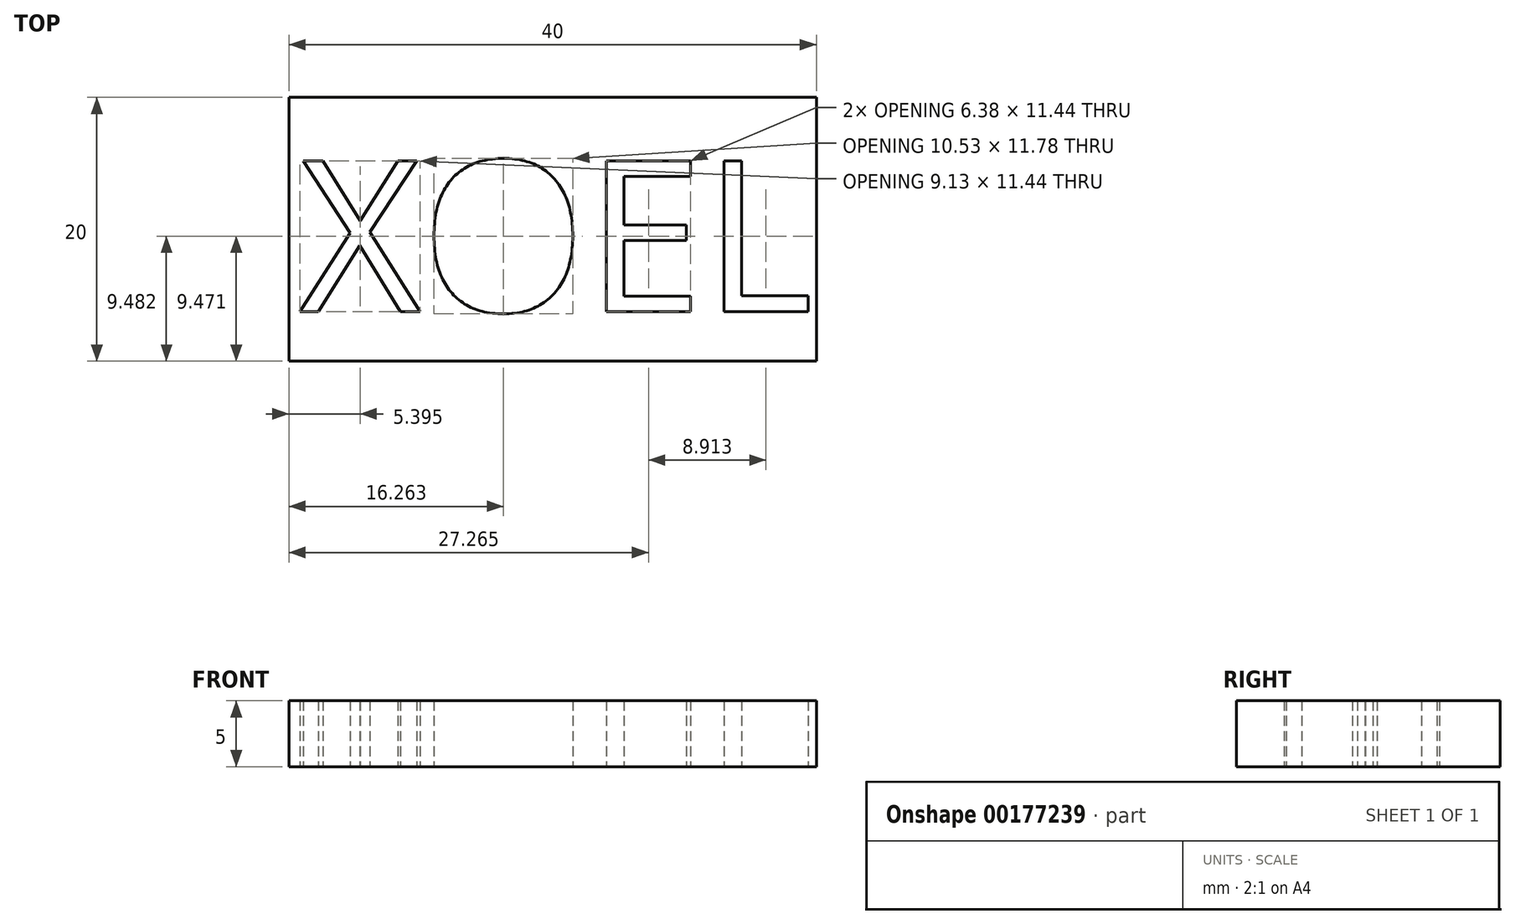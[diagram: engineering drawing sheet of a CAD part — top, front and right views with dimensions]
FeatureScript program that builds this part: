
annotation { "Feature Type Name" : "Feature", "Feature Type Description" : "" }
export const myFeature = defineFeature(function(context is Context, id is Id, definition is map)
    precondition{}
    {
        {
            var Q0;
            Q0=qCreatedBy(makeId("Top.planeOp"),FACE);
            var sketch = newSketch(context, id + "F0", { "sketchPlane" : qUnion([Q0])});
            skLineSegment(sketch, "E0.bottom", {"start": v(-40, 20) * mm, "end": v(-32.7, 20) * mm});
            skLineSegment(sketch, "E0.top", {"start": v(-40, 18) * mm, "end": v(-32.7, 18) * mm});
            skLineSegment(sketch, "E0.left", {"start": v(-32.7, 20) * mm, "end": v(-32.7, 18) * mm});
            skLineSegment(sketch, "E0.right", {"start": v(-40, 20) * mm, "end": v(-40, 18) * mm});
            skLineSegment(sketch, "E1.bottom", {"start": v(-40, 20) * mm, "end": v(0, 20) * mm});
            skLineSegment(sketch, "E1.top", {"start": v(-40, 0) * mm, "end": v(0, 0) * mm});
            skLineSegment(sketch, "E1.left", {"start": v(-40, 20) * mm, "end": v(-40, 0) * mm});
            skLineSegment(sketch, "E1.right", {"start": v(0, 20) * mm, "end": v(0, 0) * mm});
            skText(sketch, "E2", { "text": "XOEL", "fontName": "OpenSans-Regular.ttf"});
            skCircle(sketch, "E3", {"center": v(-6.92, 17.6) * mm, "radius": 2.4 * mm});
            const initialGuessF0  = {"E2": [-0.03923, 0.00375, 1, 0, 0.01154]};
            skSetInitialGuess(sketch, initialGuessF0);
            skSolve(sketch);
        }
        {
            var Q0;
            Q0 = qSketchRegion(id + "F0", true);
            extrude(context, id + "F1", {"entities" : qUnion([Q0]), "depth" : 5 * mm});
        }
    });
